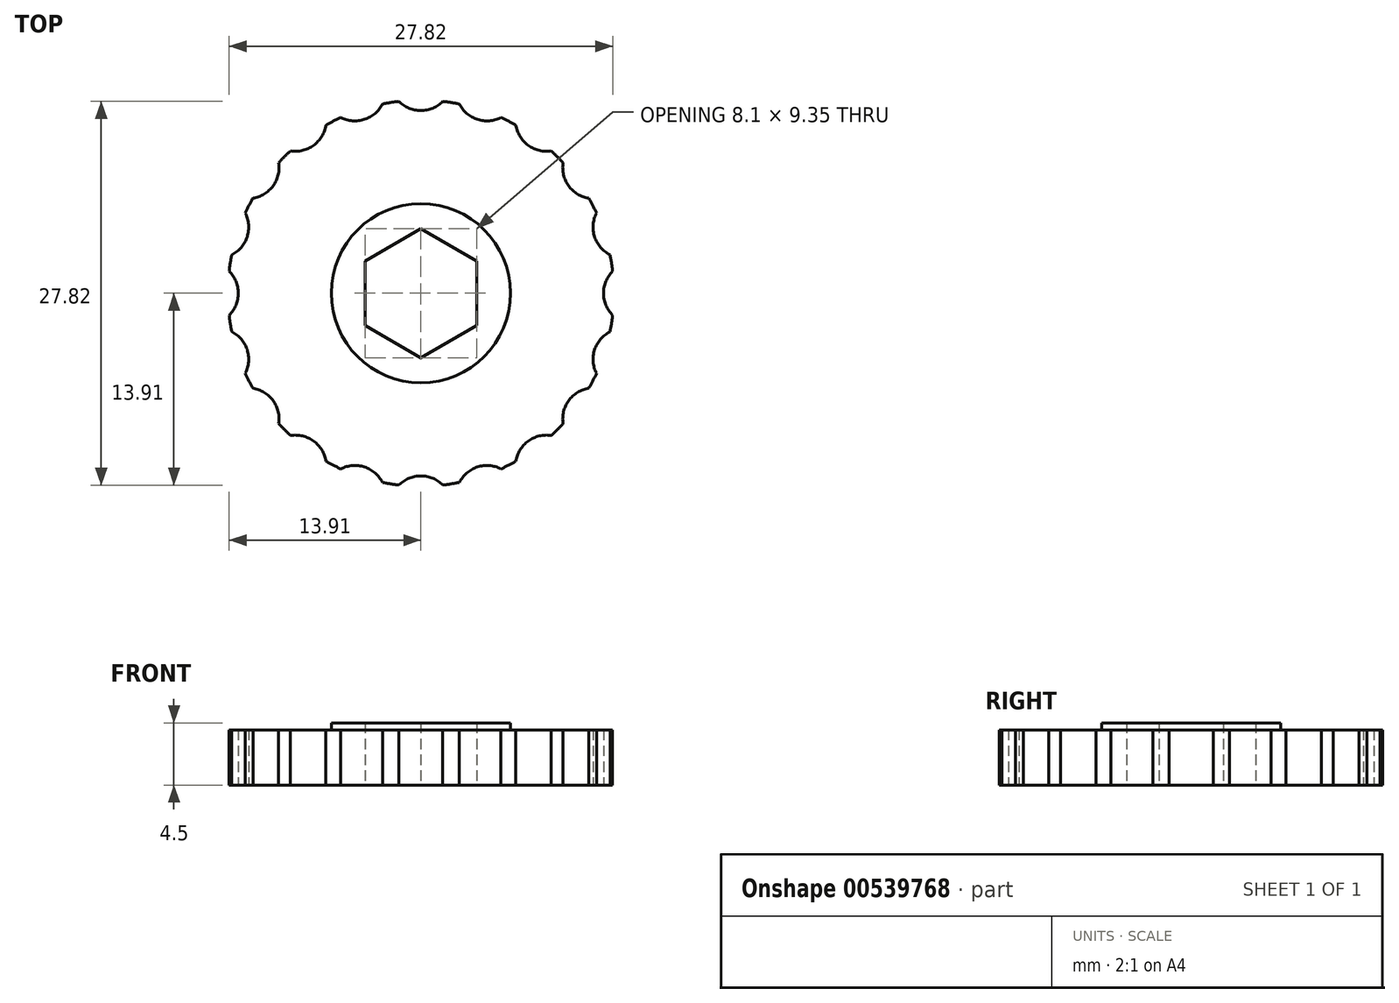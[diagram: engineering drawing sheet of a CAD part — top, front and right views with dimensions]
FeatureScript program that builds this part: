
annotation { "Feature Type Name" : "Feature", "Feature Type Description" : "" }
export const myFeature = defineFeature(function(context is Context, id is Id, definition is map)
    precondition{}
    {
        {
            var Q0;
            Q0=qCreatedBy(makeId("Top.planeOp"),FACE);
            var sketch = newSketch(context, id + "F0", { "sketchPlane" : qUnion([Q0])});
            skCircle(sketch, "E0", {"center": v(0, 0) * mm, "radius": 14 * mm});
            skCircle(sketch, "E1.cCircle", {"center": v(0, 0) * mm, "radius": 4.05 * mm, "construction": true});
            skLineSegment(sketch, "E1.0", {"start": v(4.05, -2.34) * mm, "end": v(0, -4.68) * mm});
            skLineSegment(sketch, "E1.1", {"start": v(0, -4.68) * mm, "end": v(-4.05, -2.34) * mm});
            skLineSegment(sketch, "E1.2", {"start": v(-4.05, -2.34) * mm, "end": v(-4.05, 2.34) * mm});
            skLineSegment(sketch, "E1.3", {"start": v(-4.05, 2.34) * mm, "end": v(0, 4.68) * mm});
            skLineSegment(sketch, "E1.4", {"start": v(0, 4.68) * mm, "end": v(4.05, 2.34) * mm});
            skLineSegment(sketch, "E1.5", {"start": v(4.05, 2.34) * mm, "end": v(4.05, -2.34) * mm});
            skPoint(sketch, "E1.0.midPoint", {"position": v(2.02, -3.5) * mm});
            skLineSegment(sketch, "E2", {"start": v(0, 0) * mm, "end": v(0, 4.68) * mm, "construction": true});
            skCircle(sketch, "E3", {"center": v(0, 0) * mm, "radius": 15.5 * mm});
            skCircle(sketch, "E4", {"center": v(0, 15.5) * mm, "radius": 2.25 * mm});
            skCircle(sketch, "E5.1.0", {"center": v(-4.79, 14.74) * mm, "radius": 2.25 * mm});
            skCircle(sketch, "E5.2.0", {"center": v(-9.11, 12.54) * mm, "radius": 2.25 * mm});
            skCircle(sketch, "E5.3.0", {"center": v(-12.54, 9.11) * mm, "radius": 2.25 * mm});
            skCircle(sketch, "E5.4.0", {"center": v(-14.74, 4.79) * mm, "radius": 2.25 * mm});
            skCircle(sketch, "E5.5.0", {"center": v(-15.5, 0) * mm, "radius": 2.25 * mm});
            skCircle(sketch, "E5.6.0", {"center": v(-14.74, -4.79) * mm, "radius": 2.25 * mm});
            skCircle(sketch, "E5.7.0", {"center": v(-12.54, -9.11) * mm, "radius": 2.25 * mm});
            skCircle(sketch, "E5.8.0", {"center": v(-9.11, -12.54) * mm, "radius": 2.25 * mm});
            skCircle(sketch, "E5.9.0", {"center": v(-4.79, -14.74) * mm, "radius": 2.25 * mm});
            skCircle(sketch, "E5.10.0", {"center": v(0, -15.5) * mm, "radius": 2.25 * mm});
            skCircle(sketch, "E5.11.0", {"center": v(4.79, -14.74) * mm, "radius": 2.25 * mm});
            skCircle(sketch, "E5.12.0", {"center": v(9.11, -12.54) * mm, "radius": 2.25 * mm});
            skCircle(sketch, "E5.13.0", {"center": v(12.54, -9.11) * mm, "radius": 2.25 * mm});
            skCircle(sketch, "E5.14.0", {"center": v(14.74, -4.79) * mm, "radius": 2.25 * mm});
            skCircle(sketch, "E5.15.0", {"center": v(15.5, 0) * mm, "radius": 2.25 * mm});
            skCircle(sketch, "E5.16.0", {"center": v(14.74, 4.79) * mm, "radius": 2.25 * mm});
            skCircle(sketch, "E5.17.0", {"center": v(12.54, 9.11) * mm, "radius": 2.25 * mm});
            skCircle(sketch, "E5.18.0", {"center": v(9.11, 12.54) * mm, "radius": 2.25 * mm});
            skCircle(sketch, "E5.19.0", {"center": v(4.79, 14.74) * mm, "radius": 2.25 * mm});
            skCircle(sketch, "E6", {"center": v(0, 0) * mm, "radius": 6.5 * mm});
            skSolve(sketch);
        }
        {
            var Q0;
            Q0=makeQuery(id+"F0.imprint","IMPRINT",FACE,{"disambiguationData":[TD([[makeQuery(id+"F0.imprint","IMPRINT",EDGE,{"derivedFrom":sQuery(id+"F0.wireOp",EDGE,"E6")}),-1.0]])]});
            extrude(context, id + "F1", {"entities" : qUnion([Q0]), "depth" : 4 * mm, "offsetDistance" : 25 * mm});
        }
        {
            var Q0;
            Q0=makeQuery(id+"F0.imprint","IMPRINT",FACE,{"disambiguationData":[TD([[makeQuery(id+"F0.imprint","IMPRINT",EDGE,{"derivedFrom":sQuery(id+"F0.wireOp",EDGE,"E1.0")}),1.0]])]});
            extrude(context, id + "F2", {"entities" : qUnion([Q0]), "operationType" : NewBodyOperationType.ADD, "depth" : 4.5 * mm, "offsetDistance" : 25 * mm});
        }
    });
